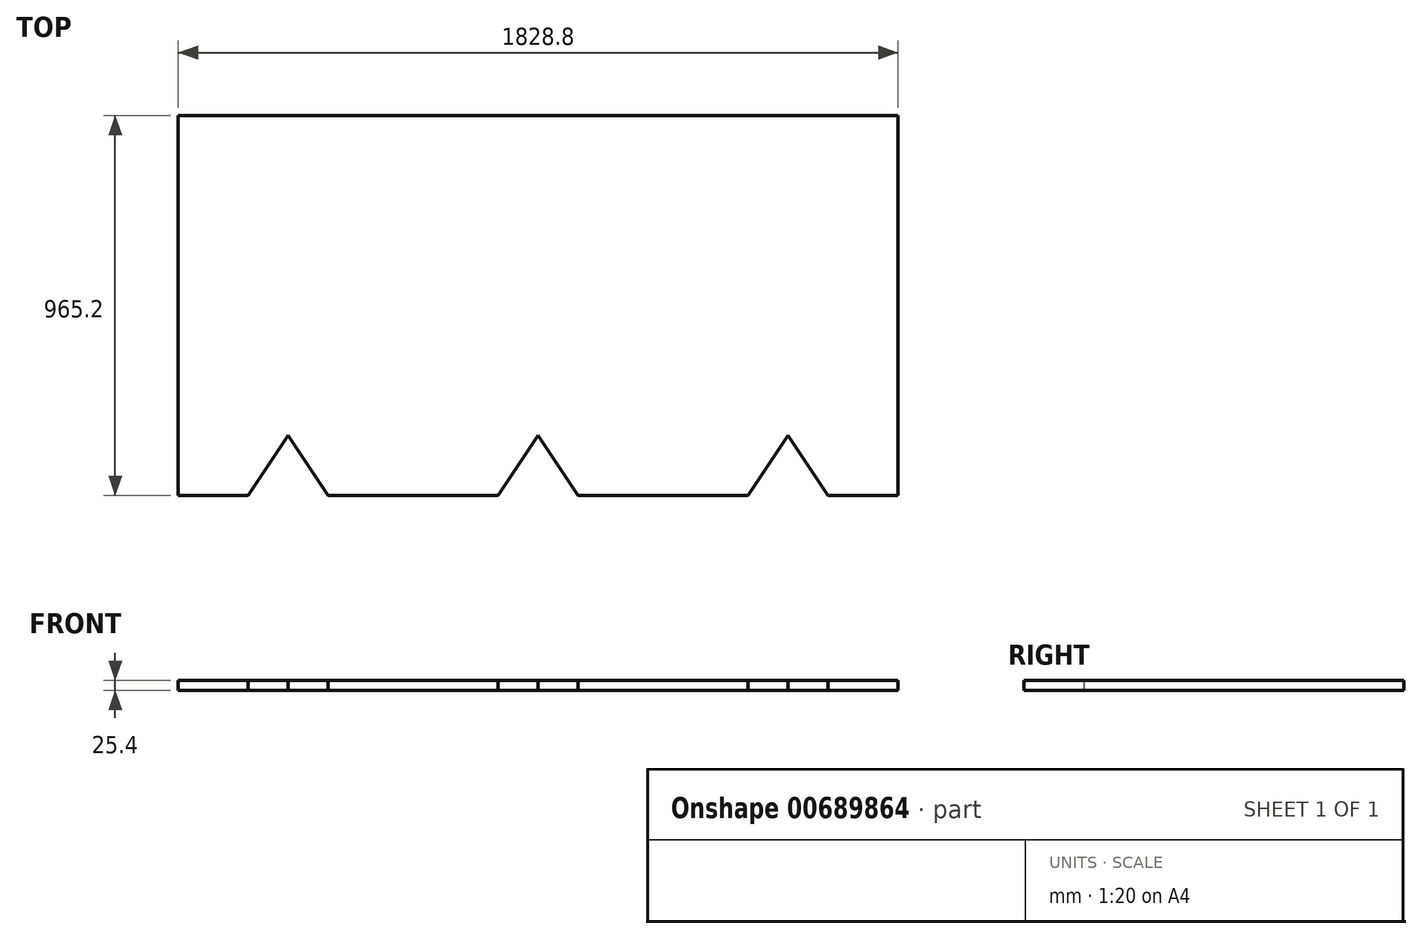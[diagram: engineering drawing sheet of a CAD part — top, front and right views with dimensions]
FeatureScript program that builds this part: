
annotation { "Feature Type Name" : "Feature", "Feature Type Description" : "" }
export const myFeature = defineFeature(function(context is Context, id is Id, definition is map)
    precondition{}
    {
        {
            var Q0;
            Q0=qCreatedBy(makeId("Top.planeOp"),FACE);
            var sketch = newSketch(context, id + "F0", { "sketchPlane" : qUnion([Q0])});
            skLineSegment(sketch, "E0", {"start": v(914.4, 0) * mm, "end": v(-914.4, 0) * mm});
            skLineSegment(sketch, "E1", {"start": v(-914.4, 0) * mm, "end": v(-914.4, -965.2) * mm});
            skLineSegment(sketch, "E2", {"start": v(-914.4, -965.2) * mm, "end": v(-736.6, -965.2) * mm});
            skLineSegment(sketch, "E3", {"start": v(-736.6, -965.2) * mm, "end": v(-635, -812.8) * mm});
            skLineSegment(sketch, "E4", {"start": v(-635, -812.8) * mm, "end": v(-533.4, -965.2) * mm});
            skLineSegment(sketch, "E5", {"start": v(0, -965.2) * mm, "end": v(0, 0) * mm, "construction": true});
            skLineSegment(sketch, "E6.MirrorCS", {"start": v(914.4, -965.2) * mm, "end": v(736.6, -965.2) * mm});
            skLineSegment(sketch, "E7.MirrorCS", {"start": v(635, -812.8) * mm, "end": v(533.4, -965.2) * mm});
            skLineSegment(sketch, "E8.MirrorCS", {"start": v(533.4, -965.2) * mm, "end": v(101.6, -965.2) * mm});
            skLineSegment(sketch, "E9.MirrorCS", {"start": v(736.6, -965.2) * mm, "end": v(635, -812.8) * mm});
            skLineSegment(sketch, "E10", {"start": v(914.4, -965.2) * mm, "end": v(914.4, 0) * mm});
            skLineSegment(sketch, "E11", {"start": v(101.6, -965.2) * mm, "end": v(0, -812.8) * mm});
            skLineSegment(sketch, "E12", {"start": v(0, -812.8) * mm, "end": v(-101.6, -965.2) * mm});
            skLineSegment(sketch, "E13", {"start": v(-101.6, -965.2) * mm, "end": v(-533.4, -965.2) * mm});
            skSolve(sketch);
        }
        {
            var Q0;
            Q0 = qSketchRegion(id + "F0", true);
            extrude(context, id + "F1", {"entities" : qUnion([Q0]), "depth" : 25.4 * mm, "offsetDistance" : 25.4 * mm});
        }
    });
